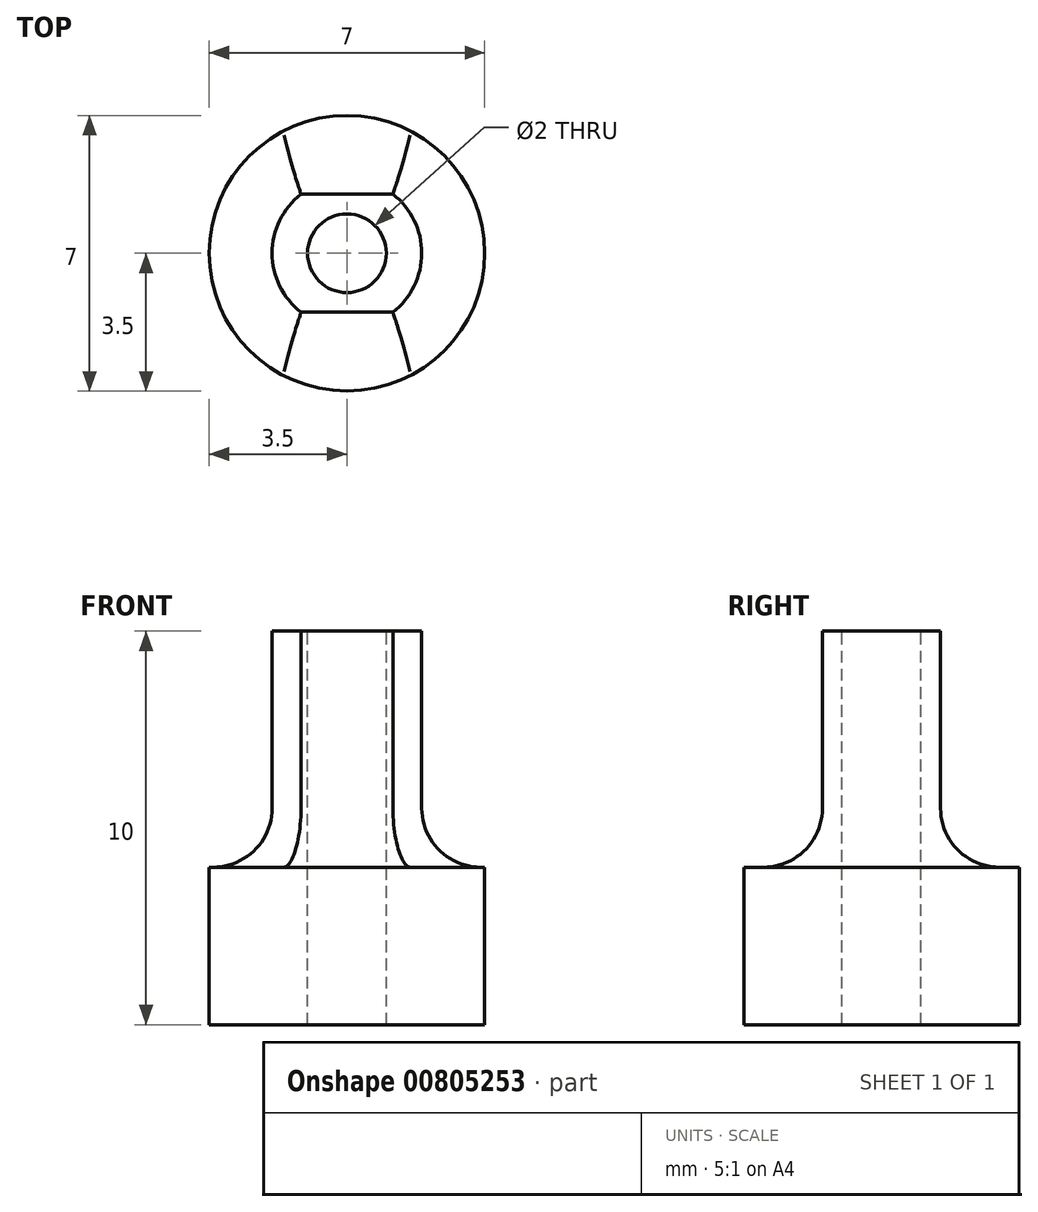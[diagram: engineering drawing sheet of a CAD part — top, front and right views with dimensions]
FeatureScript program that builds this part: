
annotation { "Feature Type Name" : "Feature", "Feature Type Description" : "" }
export const myFeature = defineFeature(function(context is Context, id is Id, definition is map)
    precondition{}
    {
        {
            var Q0;
            Q0=qCreatedBy(makeId("Top.planeOp"),FACE);
            var sketch = newSketch(context, id + "F0", { "sketchPlane" : qUnion([Q0])});
            skCircle(sketch, "E0", {"center": v(0, 0) * mm, "radius": 1.9 * mm});
            skLineSegment(sketch, "E1.bottom", {"start": v(-1.17, -1.5) * mm, "end": v(1.17, -1.5) * mm});
            skLineSegment(sketch, "E1.top", {"start": v(-1.17, 1.5) * mm, "end": v(1.17, 1.5) * mm});
            skLineSegment(sketch, "E1.left", {"start": v(-1.17, -1.5) * mm, "end": v(-1.17, 1.5) * mm});
            skLineSegment(sketch, "E1.right", {"start": v(1.17, -1.5) * mm, "end": v(1.17, 1.5) * mm});
            skSolve(sketch);
        }
        {
            var Q0;
            {var subQ0=sQuery(id+"F0.wireOp",EDGE,"E1.left");Q0=makeQuery(id+"F0.imprint","IMPRINT",FACE,{"disambiguationData":[TD([[makeQuery(id+"F0.imprint","IMPRINT",EDGE,{"derivedFrom":subQ0}),1.0]])]});}
            var Q1;
            {var subQ0=sQuery(id+"F0.wireOp",EDGE,"E1.right");Q1=makeQuery(id+"F0.imprint","IMPRINT",FACE,{"disambiguationData":[TD([[makeQuery(id+"F0.imprint","IMPRINT",EDGE,{"derivedFrom":subQ0}),-1.0]])]});}
            var Q2;
            Q2=makeQuery(id+"F0.imprint","IMPRINT",FACE,{"disambiguationData":[TD([[makeQuery(id+"F0.imprint","IMPRINT",EDGE,{"derivedFrom":sQuery(id+"F0.wireOp",EDGE,"E1.bottom")}),1.0]])]});
            extrude(context, id + "F1", {"entities" : qUnion([Q0, Q1, Q2]), "depth" : 10 * mm, "offsetDistance" : 25 * mm});
        }
        {
            var Q0;
            Q0=qCreatedBy(makeId("Top.planeOp"),FACE);
            var sketch = newSketch(context, id + "F2", { "sketchPlane" : qUnion([Q0])});
            skCircle(sketch, "E2", {"center": v(0, 0) * mm, "radius": 3.5 * mm});
            skSolve(sketch);
        }
        {
            var Q0;
            Q0=makeQuery(id+"F2.imprint","IMPRINT",FACE,{"disambiguationData":[TD([[makeQuery(id+"F2.imprint","IMPRINT",EDGE,{"derivedFrom":sQuery(id+"F2.wireOp",EDGE,"E2")}),1.0]])]});
            extrude(context, id + "F3", {"entities" : qUnion([Q0]), "operationType" : NewBodyOperationType.ADD, "depth" : 4 * mm, "offsetDistance" : 25 * mm});
        }
        {
            var Q0;
            {var subQ0=sQuery(id+"F0.wireOp",EDGE,"E1.right");var subQ1=sQuery(id+"F0.wireOp",EDGE,"E0");Q0=makeQuery(id+"F3.boolean.opBoolean","INTERSECT",EDGE,{"derivedFrom":[makeQuery(id+"F1.opExtrude","SWEPT_FACE",FACE,{"disambiguationData":[OSD([subQ1]),TDD([makeQuery(id+"F0.imprint","IMPRINT",EDGE,{"disambiguationData":[TD([[makeQuery(id+"F0.imprint","INTERSECT",VERTEX,{"derivedFrom":[subQ1,sQuery(id+"F0.wireOp",EDGE,"E1.bottom"),subQ0]}),-1.0]])],"derivedFrom":subQ1})])]}),makeQuery(id+"F3.opExtrude","CAP_FACE",FACE,{"disambiguationData":[OSD([sQuery(id+"F2.wireOp",EDGE,"E2")])],"isStart":false})]});}
            var Q1;
            {var subQ0=sQuery(id+"F0.wireOp",EDGE,"E1.left");var subQ1=sQuery(id+"F0.wireOp",EDGE,"E0");Q1=makeQuery(id+"F3.boolean.opBoolean","INTERSECT",EDGE,{"derivedFrom":[makeQuery(id+"F1.opExtrude","SWEPT_FACE",FACE,{"disambiguationData":[OSD([subQ1]),TDD([makeQuery(id+"F0.imprint","IMPRINT",EDGE,{"disambiguationData":[TD([[makeQuery(id+"F0.imprint","INTERSECT",VERTEX,{"derivedFrom":[subQ1,sQuery(id+"F0.wireOp",EDGE,"E1.bottom"),subQ0]}),1.0]])],"derivedFrom":subQ1})])]}),makeQuery(id+"F3.opExtrude","CAP_FACE",FACE,{"disambiguationData":[OSD([sQuery(id+"F2.wireOp",EDGE,"E2")])],"isStart":false})]});}
            var Q2;
            Q2=makeQuery(id+"F3.boolean.opBoolean","INTERSECT",EDGE,{"derivedFrom":[makeQuery(id+"F1.opExtrude","SWEPT_FACE",FACE,{"disambiguationData":[OSD([sQuery(id+"F0.wireOp",EDGE,"E1.top")])]}),makeQuery(id+"F3.opExtrude","CAP_FACE",FACE,{"disambiguationData":[OSD([sQuery(id+"F2.wireOp",EDGE,"E2")])],"isStart":false})]});
            var Q3;
            Q3=makeQuery(id+"F3.boolean.opBoolean","INTERSECT",EDGE,{"derivedFrom":[makeQuery(id+"F1.opExtrude","SWEPT_FACE",FACE,{"disambiguationData":[OSD([sQuery(id+"F0.wireOp",EDGE,"E1.bottom")])]}),makeQuery(id+"F3.opExtrude","CAP_FACE",FACE,{"disambiguationData":[OSD([sQuery(id+"F2.wireOp",EDGE,"E2")])],"isStart":false})]});
            fillet(context, id + "F4", {"entities" : qUnion([Q0, Q1, Q2, Q3]), "radius" : 1.5 * mm, "tangentPropagation" : true, "allowEdgeOverflow" : false});
        }
        {
            var Q0;
            Q0=makeQuery(id+"F1.opExtrude","CAP_FACE",FACE,{"disambiguationData":[OSD([sQuery(id+"F0.wireOp",EDGE,"E0"),sQuery(id+"F0.wireOp",EDGE,"E1.bottom"),sQuery(id+"F0.wireOp",EDGE,"E1.top")])],"isStart":false});
            var sketch = newSketch(context, id + "F5", { "sketchPlane" : qUnion([Q0])});
            skCircle(sketch, "E3", {"center": v(0, 0) * mm, "radius": 1 * mm});
            skSolve(sketch);
        }
        {
            var Q0;
            Q0=makeQuery(id+"F5.imprint","IMPRINT",FACE,{"disambiguationData":[TD([[makeQuery(id+"F5.imprint","IMPRINT",EDGE,{"derivedFrom":sQuery(id+"F5.wireOp",EDGE,"E3")}),1.0]])]});
            extrude(context, id + "F6", {"entities" : qUnion([Q0]), "operationType" : NewBodyOperationType.REMOVE, "oppositeDirection" : true, "depth" : 25 * mm, "offsetDistance" : 25 * mm});
        }
    });
